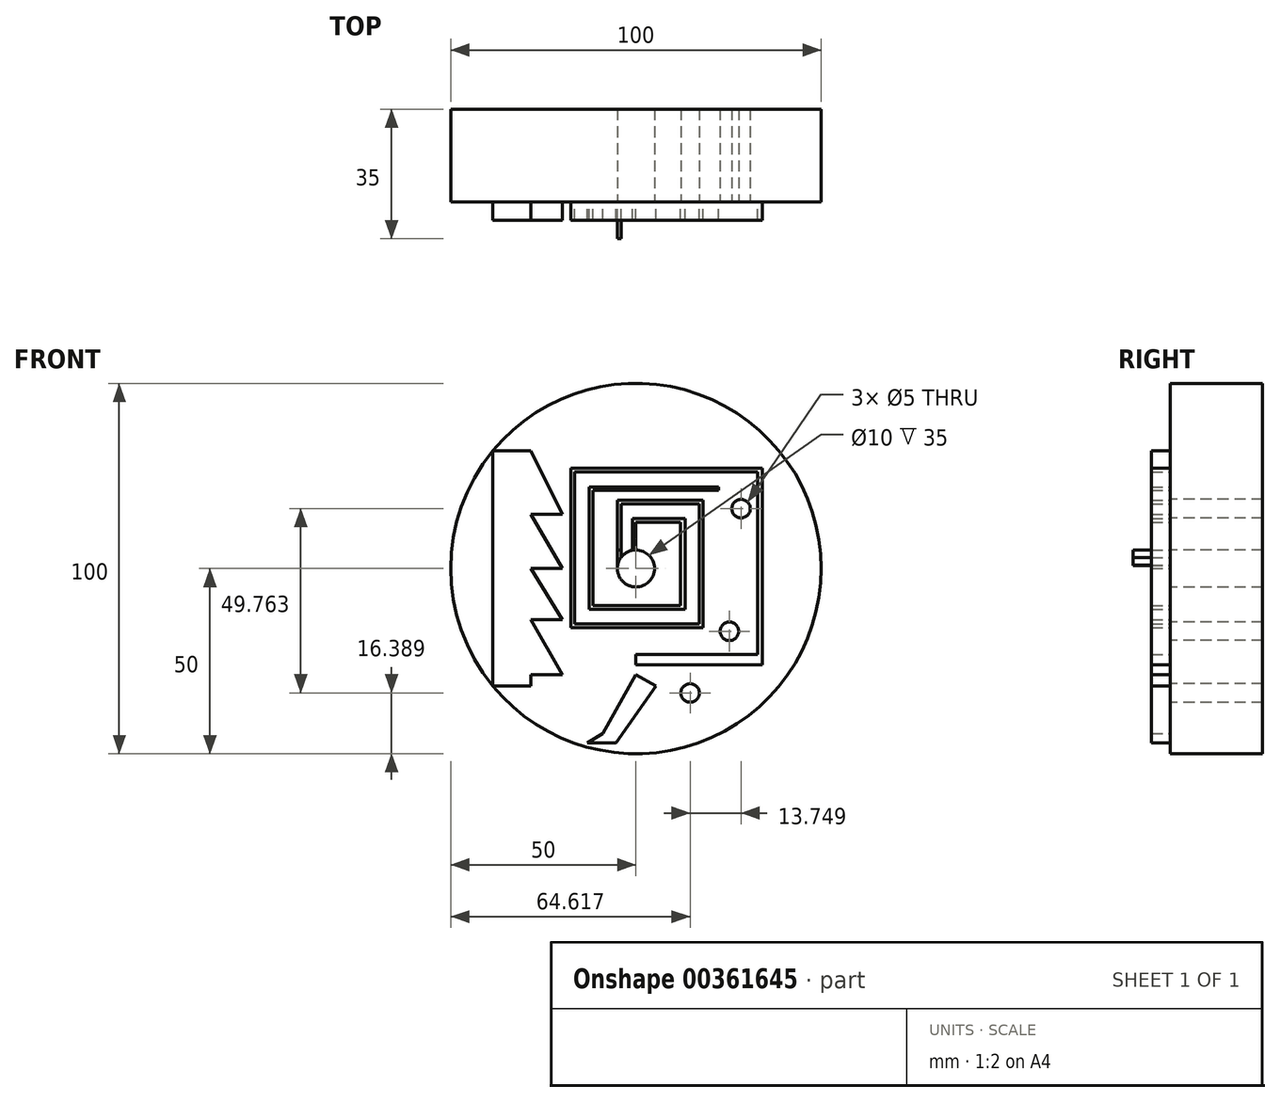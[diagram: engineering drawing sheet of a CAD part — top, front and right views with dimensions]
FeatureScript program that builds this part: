
annotation { "Feature Type Name" : "Feature", "Feature Type Description" : "" }
export const myFeature = defineFeature(function(context is Context, id is Id, definition is map)
    precondition{}
    {
        {
            var Q0;
            Q0=qCreatedBy(makeId("Front.planeOp"),FACE);
            var sketch = newSketch(context, id + "F0", { "sketchPlane" : qUnion([Q0])});
            skCircle(sketch, "E0", {"center": v(0, 0) * mm, "radius": 50 * mm});
            skSolve(sketch);
        }
        {
            var Q0;
            Q0=makeQuery(id+"F0.imprint","IMPRINT",FACE,{"disambiguationData":[TD([[makeQuery(id+"F0.imprint","IMPRINT",EDGE,{"derivedFrom":sQuery(id+"F0.wireOp",EDGE,"E0")}),1.0]])]});
            extrude(context, id + "F1", {"entities" : qUnion([Q0]), "depth" : 25 * mm});
        }
        {
            var Q0;
            Q0=makeQuery(id+"F1.opExtrude","CAP_FACE",FACE,{"disambiguationData":[OSD([sQuery(id+"F0.wireOp",EDGE,"E0")])],"isStart":false});
            var sketch = newSketch(context, id + "F2", { "sketchPlane" : qUnion([Q0])});
            skCircle(sketch, "E1", {"center": v(0, 0) * mm, "radius": 8.25 * mm});
            skSolve(sketch);
        }
        {
            var Q0;
            Q0=sQuery(id+"F2.wireOp",VERTEX,"E1.center");
            var Q1;
            Q1=makeQuery(id+"F1.opExtrude","SWEPT_BODY",BODY,{"disambiguationData":[OSD([sQuery(id+"F0.wireOp",EDGE,"E0")])]});
            hole(context, id + "F3", {"style" : HoleStyle.SIMPLE, "endStyle" : HoleEndStyle.THROUGH, "holeDiameter" : 10 * mm, "isTappedThrough" : true, "tappedDepth" : 12 * mm, "tapClearance" : 3, "locations" : qUnion([Q0]), "scope" : qUnion([Q1])});
        }
        {
            var Q0;
            Q0=makeQuery(id+"F1.opExtrude","CAP_FACE",FACE,{"disambiguationData":[OSD([sQuery(id+"F0.wireOp",EDGE,"E0")])],"isStart":false});
            var sketch = newSketch(context, id + "F4", { "sketchPlane" : qUnion([Q0])});
            skLineSegment(sketch, "E2", {"start": v(0, 5) * mm, "end": v(0, 12.48) * mm});
            skLineSegment(sketch, "E3", {"start": v(0, 12.48) * mm, "end": v(12.05, 12.48) * mm});
            skLineSegment(sketch, "E4", {"start": v(12.05, 12.48) * mm, "end": v(12.05, 0) * mm});
            skLineSegment(sketch, "E5", {"start": v(12.05, 0) * mm, "end": v(12.05, -10) * mm});
            skLineSegment(sketch, "E6", {"start": v(12.05, -10) * mm, "end": v(0, -10) * mm});
            skLineSegment(sketch, "E7", {"start": v(0, -10) * mm, "end": v(-11.6, -10) * mm});
            skLineSegment(sketch, "E8", {"start": v(-11.6, -10) * mm, "end": v(-11.6, 0) * mm});
            skLineSegment(sketch, "E9", {"start": v(-11.6, 0) * mm, "end": v(-11.6, 12.48) * mm});
            skLineSegment(sketch, "E10", {"start": v(-11.6, 12.48) * mm, "end": v(-11.6, 21.05) * mm});
            skLineSegment(sketch, "E11", {"start": v(-11.6, 21.05) * mm, "end": v(22.32, 21.05) * mm});
            skLineSegment(sketch, "E12.0", {"start": v(-16.6, 26.05) * mm, "end": v(22.32, 26.05) * mm});
            skLineSegment(sketch, "E12.1", {"start": v(-16.6, 12.48) * mm, "end": v(-16.6, 26.05) * mm});
            skLineSegment(sketch, "E12.2", {"start": v(-16.6, 0) * mm, "end": v(-16.6, 12.48) * mm});
            skLineSegment(sketch, "E12.3", {"start": v(-16.6, -15) * mm, "end": v(-16.6, 0) * mm});
            skLineSegment(sketch, "E12.4", {"start": v(0, -15) * mm, "end": v(-16.6, -15) * mm});
            skLineSegment(sketch, "E12.5", {"start": v(17.05, -15) * mm, "end": v(0, -15) * mm});
            skLineSegment(sketch, "E12.6", {"start": v(-5, 5) * mm, "end": v(-5, 17.48) * mm});
            skLineSegment(sketch, "E12.8", {"start": v(17.05, 17.48) * mm, "end": v(17.05, 0) * mm});
            skLineSegment(sketch, "E12.9", {"start": v(17.05, 0) * mm, "end": v(17.05, -15) * mm});
            skLineSegment(sketch, "E13.0", {"start": v(-16.6, 27.05) * mm, "end": v(22.32, 27.05) * mm});
            skLineSegment(sketch, "E14", {"start": v(-17.6, 26.16) * mm, "end": v(-17.6, -14.9) * mm});
            skLineSegment(sketch, "E15", {"start": v(-16.6, 27.05) * mm, "end": v(-17.6, 27.05) * mm});
            skLineSegment(sketch, "E16", {"start": v(-17.6, 27.05) * mm, "end": v(-17.6, 26.16) * mm});
            skLineSegment(sketch, "E17", {"start": v(22.32, 26.05) * mm, "end": v(22.32, 27.05) * mm});
            skLineSegment(sketch, "E18", {"start": v(-17.6, -15) * mm, "end": v(-17.6, -14.9) * mm});
            skLineSegment(sketch, "E19", {"start": v(22.32, 21.05) * mm, "end": v(22.32, 22.05) * mm});
            skLineSegment(sketch, "E20", {"start": v(22.32, 22.05) * mm, "end": v(-11.6, 22.05) * mm});
            skLineSegment(sketch, "E21", {"start": v(-11.6, 22.05) * mm, "end": v(-12.6, 22.05) * mm});
            skLineSegment(sketch, "E22", {"start": v(-12.6, 22.05) * mm, "end": v(-12.6, 5.56) * mm});
            skLineSegment(sketch, "E23", {"start": v(-12.6, 5.56) * mm, "end": v(-12.6, -11.01) * mm});
            skLineSegment(sketch, "E24", {"start": v(13.27, 12.48) * mm, "end": v(13.27, 13.48) * mm});
            skLineSegment(sketch, "E25", {"start": v(13.27, 13.48) * mm, "end": v(0, 13.48) * mm});
            skLineSegment(sketch, "E26", {"start": v(0, 13.48) * mm, "end": v(-1, 13.48) * mm});
            skLineSegment(sketch, "E27", {"start": v(-1, 13.48) * mm, "end": v(-1, 5) * mm});
            skLineSegment(sketch, "E28", {"start": v(-1, 13.48) * mm, "end": v(-1, 12.48) * mm});
            skLineSegment(sketch, "E29", {"start": v(-5, 17.48) * mm, "end": v(-5, 18.48) * mm});
            skLineSegment(sketch, "E30", {"start": v(-5, 18.48) * mm, "end": v(17.05, 18.48) * mm});
            skLineSegment(sketch, "E31", {"start": v(17.05, 18.48) * mm, "end": v(18.05, 18.48) * mm});
            skLineSegment(sketch, "E32", {"start": v(18.05, 18.48) * mm, "end": v(18.05, -15) * mm});
            skLineSegment(sketch, "E33", {"start": v(18.05, -15) * mm, "end": v(18.05, -16) * mm});
            skLineSegment(sketch, "E34", {"start": v(18.05, -16) * mm, "end": v(-17.6, -16) * mm});
            skLineSegment(sketch, "E35", {"start": v(-17.6, -16) * mm, "end": v(-17.6, -14.9) * mm});
            skLineSegment(sketch, "E36", {"start": v(13.27, 12.48) * mm, "end": v(13.27, -10) * mm});
            skLineSegment(sketch, "E37", {"start": v(13.27, -10) * mm, "end": v(13.27, -11) * mm});
            skLineSegment(sketch, "E38", {"start": v(13.27, -11) * mm, "end": v(-12.6, -11.01) * mm});
            skLineSegment(sketch, "E39", {"start": v(17.05, 17.48) * mm, "end": v(-4, 17.48) * mm});
            skLineSegment(sketch, "E40", {"start": v(-4, 17.48) * mm, "end": v(-4, 5) * mm});
            skLineSegment(sketch, "E41", {"start": v(-5, 5) * mm, "end": v(-4, 5) * mm});
            skLineSegment(sketch, "E42", {"start": v(-1, 5) * mm, "end": v(0, 5) * mm});
            skSolve(sketch);
        }
        {
            var Q0;
            Q0 = qSketchRegion(id + "F4", true);
            extrude(context, id + "F5", {"entities" : qUnion([Q0]), "operationType" : NewBodyOperationType.ADD, "depth" : 5 * mm});
        }
        {
            var Q0;
            Q0=makeQuery(id+"F1.opExtrude","CAP_FACE",FACE,{"disambiguationData":[OSD([sQuery(id+"F0.wireOp",EDGE,"E0")])],"isStart":false});
            var sketch = newSketch(context, id + "F6", { "sketchPlane" : qUnion([Q0])});
            skLineSegment(sketch, "E43", {"start": v(-5, 5) * mm, "end": v(-5, 0.76) * mm});
            skLineSegment(sketch, "E44", {"start": v(-4, 5) * mm, "end": v(-4, 3) * mm});
            skLineSegment(sketch, "E45", {"start": v(-4, 3) * mm, "end": v(-5, 0.76) * mm});
            skSolve(sketch);
        }
        {
            var Q0;
            {var subQ1=sQuery(id+"F6.wireOp",EDGE,"E43");Q0=makeQuery(id+"F6.imprint","IMPRINT",FACE,{"disambiguationData":[TD([[makeQuery(id+"F6.imprint","IMPRINT",EDGE,{"derivedFrom":subQ1}),1.0]])]});}
            extrude(context, id + "F7", {"entities" : qUnion([Q0]), "operationType" : NewBodyOperationType.ADD, "depth" : 10 * mm});
        }
        {
            var Q0;
            Q0=makeQuery(id+"F1.opExtrude","CAP_FACE",FACE,{"disambiguationData":[OSD([sQuery(id+"F0.wireOp",EDGE,"E0")])],"isStart":false});
            var sketch = newSketch(context, id + "F8", { "sketchPlane" : qUnion([Q0])});
            skLineSegment(sketch, "E46", {"start": v(22.32, 27.05) * mm, "end": v(25.6, 27.05) * mm});
            skLineSegment(sketch, "E47", {"start": v(22.32, 26.05) * mm, "end": v(25.6, 26.05) * mm});
            skLineSegment(sketch, "E48", {"start": v(22.32, 27.05) * mm, "end": v(22.32, 26.05) * mm});
            skLineSegment(sketch, "E49", {"start": v(27.15, 26.05) * mm, "end": v(25.6, 26.05) * mm});
            skLineSegment(sketch, "E50", {"start": v(25.6, 27.05) * mm, "end": v(28.47, 27.05) * mm});
            skLineSegment(sketch, "E51", {"start": v(27.15, 26.05) * mm, "end": v(28.9, 26.05) * mm});
            skLineSegment(sketch, "E52", {"start": v(28.9, 26.05) * mm, "end": v(32.89, 26.05) * mm});
            skLineSegment(sketch, "E53", {"start": v(28.47, 27.05) * mm, "end": v(32.89, 27.05) * mm});
            skLineSegment(sketch, "E54", {"start": v(32.89, 26.05) * mm, "end": v(32.89, 18.48) * mm});
            skLineSegment(sketch, "E55", {"start": v(32.89, 27.05) * mm, "end": v(34.1, 27.05) * mm});
            skLineSegment(sketch, "E56", {"start": v(34.1, 27.05) * mm, "end": v(34.1, 18.48) * mm});
            skLineSegment(sketch, "E57", {"start": v(34.1, 18.48) * mm, "end": v(34.1, 11.97) * mm});
            skLineSegment(sketch, "E58", {"start": v(32.89, 18.48) * mm, "end": v(32.89, 9.35) * mm});
            skLineSegment(sketch, "E59", {"start": v(34.1, 11.97) * mm, "end": v(34.1, 6.97) * mm});
            skLineSegment(sketch, "E60", {"start": v(32.89, 9.35) * mm, "end": v(32.89, 5.56) * mm});
            skLineSegment(sketch, "E61", {"start": v(34.1, 6.97) * mm, "end": v(34.1, 0) * mm});
            skLineSegment(sketch, "E62", {"start": v(32.89, 5.56) * mm, "end": v(32.89, 0) * mm});
            skLineSegment(sketch, "E63", {"start": v(32.89, 0) * mm, "end": v(32.89, -5.78) * mm});
            skLineSegment(sketch, "E64", {"start": v(34.1, 0) * mm, "end": v(34.1, -16) * mm});
            skLineSegment(sketch, "E65", {"start": v(32.89, -5.78) * mm, "end": v(32.89, -17.55) * mm});
            skLineSegment(sketch, "E66", {"start": v(32.89, -17.55) * mm, "end": v(32.89, -21.47) * mm});
            skLineSegment(sketch, "E67", {"start": v(34.1, -16) * mm, "end": v(34.1, -23.27) * mm});
            skLineSegment(sketch, "E68", {"start": v(32.89, -21.47) * mm, "end": v(32.89, -23.27) * mm});
            skLineSegment(sketch, "E69", {"start": v(32.89, -23.27) * mm, "end": v(34.1, -23.27) * mm});
            skSolve(sketch);
        }
        {
            var Q0;
            Q0 = qSketchRegion(id + "F8", true);
            extrude(context, id + "F9", {"entities" : qUnion([Q0]), "operationType" : NewBodyOperationType.ADD, "depth" : 5 * mm});
        }
        {
            var Q0;
            Q0=makeQuery(id+"F1.opExtrude","CAP_FACE",FACE,{"disambiguationData":[OSD([sQuery(id+"F0.wireOp",EDGE,"E0")])],"isStart":false});
            var sketch = newSketch(context, id + "F10", { "sketchPlane" : qUnion([Q0])});
            skLineSegment(sketch, "E70", {"start": v(32.89, -23.27) * mm, "end": v(0, -23.27) * mm});
            skLineSegment(sketch, "E71", {"start": v(34.1, -23.27) * mm, "end": v(34.1, -26.04) * mm});
            skLineSegment(sketch, "E72", {"start": v(34.1, -26.04) * mm, "end": v(0, -26.04) * mm});
            skLineSegment(sketch, "E73", {"start": v(0, -26.04) * mm, "end": v(0, -23.27) * mm});
            skLineSegment(sketch, "E74", {"start": v(32.89, -23.27) * mm, "end": v(34.1, -23.27) * mm});
            skSolve(sketch);
        }
        {
            var Q0;
            Q0=makeQuery(id+"F10.imprint","IMPRINT",FACE,{"disambiguationData":[TD([[makeQuery(id+"F10.imprint","IMPRINT",EDGE,{"derivedFrom":sQuery(id+"F10.wireOp",EDGE,"E70")}),1.0]])]});
            extrude(context, id + "F11", {"entities" : qUnion([Q0]), "operationType" : NewBodyOperationType.ADD, "depth" : 5 * mm});
        }
        {
            var Q0;
            Q0=makeQuery(id+"F1.opExtrude","CAP_FACE",FACE,{"disambiguationData":[OSD([sQuery(id+"F0.wireOp",EDGE,"E0")])],"isStart":false});
            var sketch = newSketch(context, id + "F12", { "sketchPlane" : qUnion([Q0])});
            skCircle(sketch, "E75", {"center": v(25.22, -16.96) * mm, "radius": 3.33 * mm});
            skCircle(sketch, "E76", {"center": v(28.37, 16.15) * mm, "radius": 2.9 * mm});
            skSolve(sketch);
        }
        {
            var Q0;
            Q0=sQuery(id+"F12.wireOp",VERTEX,"E75.center");
            var Q1;
            Q1=sQuery(id+"F12.wireOp",VERTEX,"E76.center");
            var Q2;
            Q2=makeQuery(id+"F1.opExtrude","SWEPT_BODY",BODY,{"disambiguationData":[OSD([sQuery(id+"F0.wireOp",EDGE,"E0")])]});
            hole(context, id + "F13", {"style" : HoleStyle.SIMPLE, "endStyle" : HoleEndStyle.THROUGH, "holeDiameter" : 5 * mm, "isTappedThrough" : true, "tappedDepth" : 12 * mm, "tapClearance" : 3, "locations" : qUnion([Q0, Q1]), "scope" : qUnion([Q2])});
        }
        {
            var Q0;
            Q0=makeQuery(id+"F1.opExtrude","CAP_FACE",FACE,{"disambiguationData":[OSD([sQuery(id+"F0.wireOp",EDGE,"E0")])],"isStart":false});
            var sketch = newSketch(context, id + "F14", { "sketchPlane" : qUnion([Q0])});
            skLineSegment(sketch, "E77", {"start": v(-38.64, 31.73) * mm, "end": v(-38.64, -31.73) * mm});
            skLineSegment(sketch, "E78", {"start": v(-38.64, 31.73) * mm, "end": v(-28.42, 31.73) * mm});
            skLineSegment(sketch, "E79", {"start": v(-28.42, 31.73) * mm, "end": v(-28.42, -31.03) * mm});
            skLineSegment(sketch, "E80", {"start": v(-38.64, -31.73) * mm, "end": v(-28.42, -31.73) * mm});
            skLineSegment(sketch, "E81", {"start": v(-28.42, -31.03) * mm, "end": v(-28.42, -31.73) * mm});
            skSolve(sketch);
        }
        {
            var Q0;
            Q0 = qSketchRegion(id + "F14", true);
            extrude(context, id + "F15", {"entities" : qUnion([Q0]), "operationType" : NewBodyOperationType.ADD, "depth" : 5 * mm});
        }
        {
            var Q0;
            {var subQ0=sQuery(id+"F0.wireOp",EDGE,"E0");var subQ1=makeQuery(id+"F1.opExtrude","CAP_FACE",FACE,{"disambiguationData":[OSD([subQ0])],"isStart":false});var subQ2=sQuery(id+"F3.hole-0.sketch.wireOp",EDGE,"core_line_2");Q0=makeQuery(id+"F15.boolean.opBoolean","SPLIT",FACE,{"disambiguationData":[TD([makeQuery(id+"F1.opExtrude","SWEPT_FACE",FACE,{"disambiguationData":[OSD([subQ0])]}),subQ1,makeQuery(id+"F3.hole-0.boolean.opBoolean","COPY",FACE,{"derivedFrom":makeQuery(id+"F3.hole-0.opRevolve","SWEPT_FACE",FACE,{"disambiguationData":[OSD([subQ2])]})}),makeQuery(id+"F5.opExtrude","SWEPT_FACE",FACE,{"disambiguationData":[OSD([sQuery(id+"F4.wireOp",EDGE,"E2")])]}),makeQuery(id+"F5.opExtrude","SWEPT_FACE",FACE,{"disambiguationData":[OSD([sQuery(id+"F4.wireOp",EDGE,"E3")])]}),makeQuery(id+"F5.opExtrude","SWEPT_FACE",FACE,{"disambiguationData":[OSD([sQuery(id+"F4.wireOp",EDGE,"E4"),sQuery(id+"F4.wireOp",EDGE,"E5")])]}),makeQuery(id+"F5.opExtrude","SWEPT_FACE",FACE,{"disambiguationData":[OSD([sQuery(id+"F4.wireOp",EDGE,"E6"),sQuery(id+"F4.wireOp",EDGE,"E7")])]}),makeQuery(id+"F5.opExtrude","SWEPT_FACE",FACE,{"disambiguationData":[OSD([sQuery(id+"F4.wireOp",EDGE,"E8"),sQuery(id+"F4.wireOp",EDGE,"E9"),sQuery(id+"F4.wireOp",EDGE,"E10")])]}),makeQuery(id+"F5.opExtrude","SWEPT_FACE",FACE,{"disambiguationData":[OSD([sQuery(id+"F4.wireOp",EDGE,"E11")])]}),makeQuery(id+"F5.opExtrude","SWEPT_FACE",FACE,{"disambiguationData":[OSD([sQuery(id+"F4.wireOp",EDGE,"E12.0")])]}),makeQuery(id+"F5.opExtrude","SWEPT_FACE",FACE,{"disambiguationData":[OSD([sQuery(id+"F4.wireOp",EDGE,"E12.1"),sQuery(id+"F4.wireOp",EDGE,"E12.2"),sQuery(id+"F4.wireOp",EDGE,"E12.3")])]}),makeQuery(id+"F5.opExtrude","SWEPT_FACE",FACE,{"disambiguationData":[OSD([sQuery(id+"F4.wireOp",EDGE,"E12.4"),sQuery(id+"F4.wireOp",EDGE,"E12.5")])]}),makeQuery(id+"F5.opExtrude","SWEPT_FACE",FACE,{"disambiguationData":[OSD([sQuery(id+"F4.wireOp",EDGE,"E12.6"),sQuery(id+"F4.wireOp",EDGE,"E29")])]}),makeQuery(id+"F5.opExtrude","SWEPT_FACE",FACE,{"disambiguationData":[OSD([sQuery(id+"F4.wireOp",EDGE,"E12.8"),sQuery(id+"F4.wireOp",EDGE,"E12.9")])]}),makeQuery(id+"F5.opExtrude","SWEPT_FACE",FACE,{"disambiguationData":[OSD([sQuery(id+"F4.wireOp",EDGE,"E13.0"),sQuery(id+"F4.wireOp",EDGE,"E15")])]}),makeQuery(id+"F5.opExtrude","SWEPT_FACE",FACE,{"disambiguationData":[OSD([sQuery(id+"F4.wireOp",EDGE,"E14"),sQuery(id+"F4.wireOp",EDGE,"E16"),sQuery(id+"F4.wireOp",EDGE,"E35")])]}),makeQuery(id+"F5.opExtrude","SWEPT_FACE",FACE,{"disambiguationData":[OSD([sQuery(id+"F4.wireOp",EDGE,"E19")])]}),makeQuery(id+"F5.opExtrude","SWEPT_FACE",FACE,{"disambiguationData":[OSD([sQuery(id+"F4.wireOp",EDGE,"E20"),sQuery(id+"F4.wireOp",EDGE,"E21")])]}),makeQuery(id+"F5.opExtrude","SWEPT_FACE",FACE,{"disambiguationData":[OSD([sQuery(id+"F4.wireOp",EDGE,"E22"),sQuery(id+"F4.wireOp",EDGE,"E23")])]}),makeQuery(id+"F5.opExtrude","SWEPT_FACE",FACE,{"disambiguationData":[OSD([sQuery(id+"F4.wireOp",EDGE,"E24"),sQuery(id+"F4.wireOp",EDGE,"E36"),sQuery(id+"F4.wireOp",EDGE,"E37")])]}),makeQuery(id+"F5.opExtrude","SWEPT_FACE",FACE,{"disambiguationData":[OSD([sQuery(id+"F4.wireOp",EDGE,"E25"),sQuery(id+"F4.wireOp",EDGE,"E26")])]}),makeQuery(id+"F5.opExtrude","SWEPT_FACE",FACE,{"disambiguationData":[OSD([sQuery(id+"F4.wireOp",EDGE,"E27"),sQuery(id+"F4.wireOp",EDGE,"E28")])]}),makeQuery(id+"F5.opExtrude","SWEPT_FACE",FACE,{"disambiguationData":[OSD([sQuery(id+"F4.wireOp",EDGE,"E30"),sQuery(id+"F4.wireOp",EDGE,"E31")])]}),makeQuery(id+"F5.opExtrude","SWEPT_FACE",FACE,{"disambiguationData":[OSD([sQuery(id+"F4.wireOp",EDGE,"E32"),sQuery(id+"F4.wireOp",EDGE,"E33")])]}),makeQuery(id+"F5.opExtrude","SWEPT_FACE",FACE,{"disambiguationData":[OSD([sQuery(id+"F4.wireOp",EDGE,"E34")])]}),makeQuery(id+"F5.opExtrude","SWEPT_FACE",FACE,{"disambiguationData":[OSD([sQuery(id+"F4.wireOp",EDGE,"E38")])]}),makeQuery(id+"F5.opExtrude","SWEPT_FACE",FACE,{"disambiguationData":[OSD([sQuery(id+"F4.wireOp",EDGE,"E39")])]}),makeQuery(id+"F5.opExtrude","SWEPT_FACE",FACE,{"disambiguationData":[OSD([sQuery(id+"F4.wireOp",EDGE,"E40")])]}),makeQuery(id+"F5.opExtrude","SWEPT_FACE",FACE,{"disambiguationData":[OSD([sQuery(id+"F4.wireOp",EDGE,"E42")])]}),makeQuery(id+"F7.opExtrude","SWEPT_FACE",FACE,{"disambiguationData":[OSD([sQuery(id+"F6.wireOp",EDGE,"E43")])]}),makeQuery(id+"F7.opExtrude","SWEPT_FACE",FACE,{"disambiguationData":[OSD([sQuery(id+"F6.wireOp",EDGE,"E44")])]}),makeQuery(id+"F7.opExtrude","SWEPT_FACE",FACE,{"disambiguationData":[OSD([sQuery(id+"F6.wireOp",EDGE,"E45")])]}),makeQuery(id+"F7.opExtrude","SWEPT_FACE",FACE,{"disambiguationData":[OSD([subQ2,sQuery(id+"F3.hole-0.sketch.wireOp",EDGE,"core_line_3")])]}),makeQuery(id+"F9.opExtrude","SWEPT_FACE",FACE,{"disambiguationData":[OSD([sQuery(id+"F8.wireOp",EDGE,"E46"),sQuery(id+"F8.wireOp",EDGE,"E50"),sQuery(id+"F8.wireOp",EDGE,"E53"),sQuery(id+"F8.wireOp",EDGE,"E55")])]}),makeQuery(id+"F9.opExtrude","SWEPT_FACE",FACE,{"disambiguationData":[OSD([sQuery(id+"F8.wireOp",EDGE,"E47"),sQuery(id+"F8.wireOp",EDGE,"E49"),sQuery(id+"F8.wireOp",EDGE,"E51"),sQuery(id+"F8.wireOp",EDGE,"E52")])]}),makeQuery(id+"F9.opExtrude","SWEPT_FACE",FACE,{"disambiguationData":[OSD([sQuery(id+"F8.wireOp",EDGE,"E54"),sQuery(id+"F8.wireOp",EDGE,"E58"),sQuery(id+"F8.wireOp",EDGE,"E60"),sQuery(id+"F8.wireOp",EDGE,"E62"),sQuery(id+"F8.wireOp",EDGE,"E63"),sQuery(id+"F8.wireOp",EDGE,"E65"),sQuery(id+"F8.wireOp",EDGE,"E66"),sQuery(id+"F8.wireOp",EDGE,"E68")])]}),makeQuery(id+"F9.opExtrude","SWEPT_FACE",FACE,{"disambiguationData":[OSD([sQuery(id+"F8.wireOp",EDGE,"E56"),sQuery(id+"F8.wireOp",EDGE,"E57"),sQuery(id+"F8.wireOp",EDGE,"E59"),sQuery(id+"F8.wireOp",EDGE,"E61"),sQuery(id+"F8.wireOp",EDGE,"E64"),sQuery(id+"F8.wireOp",EDGE,"E67")])]}),makeQuery(id+"F11.opExtrude","SWEPT_FACE",FACE,{"disambiguationData":[OSD([sQuery(id+"F10.wireOp",EDGE,"E70"),sQuery(id+"F10.wireOp",EDGE,"E74")])]}),makeQuery(id+"F11.opExtrude","SWEPT_FACE",FACE,{"disambiguationData":[OSD([sQuery(id+"F10.wireOp",EDGE,"E71")])]}),makeQuery(id+"F11.opExtrude","SWEPT_FACE",FACE,{"disambiguationData":[OSD([sQuery(id+"F10.wireOp",EDGE,"E72")])]}),makeQuery(id+"F11.opExtrude","SWEPT_FACE",FACE,{"disambiguationData":[OSD([sQuery(id+"F10.wireOp",EDGE,"E73")])]}),makeQuery(id+"F13.hole-0.boolean.opBoolean","COPY",FACE,{"derivedFrom":makeQuery(id+"F13.hole-0.opRevolve","SWEPT_FACE",FACE,{"disambiguationData":[OSD([sQuery(id+"F13.hole-0.sketch.wireOp",EDGE,"core_line_2")])]})}),makeQuery(id+"F13.hole-1.boolean.opBoolean","COPY",FACE,{"derivedFrom":makeQuery(id+"F13.hole-1.opRevolve","SWEPT_FACE",FACE,{"disambiguationData":[OSD([sQuery(id+"F13.hole-1.sketch.wireOp",EDGE,"core_line_2")])]})}),makeQuery(id+"F15.opExtrude","SWEPT_FACE",FACE,{"disambiguationData":[OSD([sQuery(id+"F14.wireOp",EDGE,"E77")])]}),makeQuery(id+"F15.opExtrude","SWEPT_FACE",FACE,{"disambiguationData":[OSD([sQuery(id+"F14.wireOp",EDGE,"E78")])]}),makeQuery(id+"F15.opExtrude","SWEPT_FACE",FACE,{"disambiguationData":[OSD([sQuery(id+"F14.wireOp",EDGE,"E79"),sQuery(id+"F14.wireOp",EDGE,"E81")])]}),makeQuery(id+"F15.opExtrude","SWEPT_FACE",FACE,{"disambiguationData":[OSD([sQuery(id+"F14.wireOp",EDGE,"E80")])]})])],"derivedFrom":subQ1});}
            var sketch = newSketch(context, id + "F16", { "sketchPlane" : qUnion([Q0])});
            skLineSegment(sketch, "E82", {"start": v(-28.42, 31.73) * mm, "end": v(-19.87, 14.57) * mm});
            skLineSegment(sketch, "E83", {"start": v(-28.42, 31.73) * mm, "end": v(-28.42, 14.57) * mm});
            skLineSegment(sketch, "E84", {"start": v(-28.42, 14.57) * mm, "end": v(-19.87, 14.57) * mm});
            skLineSegment(sketch, "E85", {"start": v(-28.42, 14.57) * mm, "end": v(-28.42, 0) * mm});
            skLineSegment(sketch, "E86", {"start": v(-28.42, 0) * mm, "end": v(-19.87, 0) * mm});
            skLineSegment(sketch, "E87", {"start": v(-19.87, 0) * mm, "end": v(-28.42, 14.57) * mm});
            skLineSegment(sketch, "E88", {"start": v(-28.42, 0) * mm, "end": v(-28.42, -13.84) * mm});
            skLineSegment(sketch, "E89", {"start": v(-28.42, -13.84) * mm, "end": v(-19.87, -13.84) * mm});
            skLineSegment(sketch, "E90", {"start": v(-19.87, -13.84) * mm, "end": v(-28.42, 0) * mm});
            skLineSegment(sketch, "E91", {"start": v(-28.42, -13.84) * mm, "end": v(-28.42, -28.66) * mm});
            skLineSegment(sketch, "E92", {"start": v(-28.42, -28.66) * mm, "end": v(-19.87, -28.66) * mm});
            skLineSegment(sketch, "E93", {"start": v(-19.87, -28.66) * mm, "end": v(-28.42, -13.84) * mm});
            skSolve(sketch);
        }
        {
            var Q0;
            Q0 = qSketchRegion(id + "F16", true);
            extrude(context, id + "F17", {"entities" : qUnion([Q0]), "operationType" : NewBodyOperationType.ADD, "depth" : 5 * mm});
        }
        {
            var Q0;
            {var subQ0=sQuery(id+"F0.wireOp",EDGE,"E0");var subQ1=makeQuery(id+"F1.opExtrude","CAP_FACE",FACE,{"disambiguationData":[OSD([subQ0])],"isStart":false});var subQ2=sQuery(id+"F3.hole-0.sketch.wireOp",EDGE,"core_line_2");Q0=makeQuery(id+"F15.boolean.opBoolean","SPLIT",FACE,{"disambiguationData":[TD([makeQuery(id+"F1.opExtrude","SWEPT_FACE",FACE,{"disambiguationData":[OSD([subQ0])]}),subQ1,makeQuery(id+"F3.hole-0.boolean.opBoolean","COPY",FACE,{"derivedFrom":makeQuery(id+"F3.hole-0.opRevolve","SWEPT_FACE",FACE,{"disambiguationData":[OSD([subQ2])]})}),makeQuery(id+"F5.opExtrude","SWEPT_FACE",FACE,{"disambiguationData":[OSD([sQuery(id+"F4.wireOp",EDGE,"E2")])]}),makeQuery(id+"F5.opExtrude","SWEPT_FACE",FACE,{"disambiguationData":[OSD([sQuery(id+"F4.wireOp",EDGE,"E3")])]}),makeQuery(id+"F5.opExtrude","SWEPT_FACE",FACE,{"disambiguationData":[OSD([sQuery(id+"F4.wireOp",EDGE,"E4"),sQuery(id+"F4.wireOp",EDGE,"E5")])]}),makeQuery(id+"F5.opExtrude","SWEPT_FACE",FACE,{"disambiguationData":[OSD([sQuery(id+"F4.wireOp",EDGE,"E6"),sQuery(id+"F4.wireOp",EDGE,"E7")])]}),makeQuery(id+"F5.opExtrude","SWEPT_FACE",FACE,{"disambiguationData":[OSD([sQuery(id+"F4.wireOp",EDGE,"E8"),sQuery(id+"F4.wireOp",EDGE,"E9"),sQuery(id+"F4.wireOp",EDGE,"E10")])]}),makeQuery(id+"F5.opExtrude","SWEPT_FACE",FACE,{"disambiguationData":[OSD([sQuery(id+"F4.wireOp",EDGE,"E11")])]}),makeQuery(id+"F5.opExtrude","SWEPT_FACE",FACE,{"disambiguationData":[OSD([sQuery(id+"F4.wireOp",EDGE,"E12.0")])]}),makeQuery(id+"F5.opExtrude","SWEPT_FACE",FACE,{"disambiguationData":[OSD([sQuery(id+"F4.wireOp",EDGE,"E12.1"),sQuery(id+"F4.wireOp",EDGE,"E12.2"),sQuery(id+"F4.wireOp",EDGE,"E12.3")])]}),makeQuery(id+"F5.opExtrude","SWEPT_FACE",FACE,{"disambiguationData":[OSD([sQuery(id+"F4.wireOp",EDGE,"E12.4"),sQuery(id+"F4.wireOp",EDGE,"E12.5")])]}),makeQuery(id+"F5.opExtrude","SWEPT_FACE",FACE,{"disambiguationData":[OSD([sQuery(id+"F4.wireOp",EDGE,"E12.6"),sQuery(id+"F4.wireOp",EDGE,"E29")])]}),makeQuery(id+"F5.opExtrude","SWEPT_FACE",FACE,{"disambiguationData":[OSD([sQuery(id+"F4.wireOp",EDGE,"E12.8"),sQuery(id+"F4.wireOp",EDGE,"E12.9")])]}),makeQuery(id+"F5.opExtrude","SWEPT_FACE",FACE,{"disambiguationData":[OSD([sQuery(id+"F4.wireOp",EDGE,"E13.0"),sQuery(id+"F4.wireOp",EDGE,"E15")])]}),makeQuery(id+"F5.opExtrude","SWEPT_FACE",FACE,{"disambiguationData":[OSD([sQuery(id+"F4.wireOp",EDGE,"E14"),sQuery(id+"F4.wireOp",EDGE,"E16"),sQuery(id+"F4.wireOp",EDGE,"E35")])]}),makeQuery(id+"F5.opExtrude","SWEPT_FACE",FACE,{"disambiguationData":[OSD([sQuery(id+"F4.wireOp",EDGE,"E19")])]}),makeQuery(id+"F5.opExtrude","SWEPT_FACE",FACE,{"disambiguationData":[OSD([sQuery(id+"F4.wireOp",EDGE,"E20"),sQuery(id+"F4.wireOp",EDGE,"E21")])]}),makeQuery(id+"F5.opExtrude","SWEPT_FACE",FACE,{"disambiguationData":[OSD([sQuery(id+"F4.wireOp",EDGE,"E22"),sQuery(id+"F4.wireOp",EDGE,"E23")])]}),makeQuery(id+"F5.opExtrude","SWEPT_FACE",FACE,{"disambiguationData":[OSD([sQuery(id+"F4.wireOp",EDGE,"E24"),sQuery(id+"F4.wireOp",EDGE,"E36"),sQuery(id+"F4.wireOp",EDGE,"E37")])]}),makeQuery(id+"F5.opExtrude","SWEPT_FACE",FACE,{"disambiguationData":[OSD([sQuery(id+"F4.wireOp",EDGE,"E25"),sQuery(id+"F4.wireOp",EDGE,"E26")])]}),makeQuery(id+"F5.opExtrude","SWEPT_FACE",FACE,{"disambiguationData":[OSD([sQuery(id+"F4.wireOp",EDGE,"E27"),sQuery(id+"F4.wireOp",EDGE,"E28")])]}),makeQuery(id+"F5.opExtrude","SWEPT_FACE",FACE,{"disambiguationData":[OSD([sQuery(id+"F4.wireOp",EDGE,"E30"),sQuery(id+"F4.wireOp",EDGE,"E31")])]}),makeQuery(id+"F5.opExtrude","SWEPT_FACE",FACE,{"disambiguationData":[OSD([sQuery(id+"F4.wireOp",EDGE,"E32"),sQuery(id+"F4.wireOp",EDGE,"E33")])]}),makeQuery(id+"F5.opExtrude","SWEPT_FACE",FACE,{"disambiguationData":[OSD([sQuery(id+"F4.wireOp",EDGE,"E34")])]}),makeQuery(id+"F5.opExtrude","SWEPT_FACE",FACE,{"disambiguationData":[OSD([sQuery(id+"F4.wireOp",EDGE,"E38")])]}),makeQuery(id+"F5.opExtrude","SWEPT_FACE",FACE,{"disambiguationData":[OSD([sQuery(id+"F4.wireOp",EDGE,"E39")])]}),makeQuery(id+"F5.opExtrude","SWEPT_FACE",FACE,{"disambiguationData":[OSD([sQuery(id+"F4.wireOp",EDGE,"E40")])]}),makeQuery(id+"F5.opExtrude","SWEPT_FACE",FACE,{"disambiguationData":[OSD([sQuery(id+"F4.wireOp",EDGE,"E42")])]}),makeQuery(id+"F7.opExtrude","SWEPT_FACE",FACE,{"disambiguationData":[OSD([sQuery(id+"F6.wireOp",EDGE,"E43")])]}),makeQuery(id+"F7.opExtrude","SWEPT_FACE",FACE,{"disambiguationData":[OSD([sQuery(id+"F6.wireOp",EDGE,"E44")])]}),makeQuery(id+"F7.opExtrude","SWEPT_FACE",FACE,{"disambiguationData":[OSD([sQuery(id+"F6.wireOp",EDGE,"E45")])]}),makeQuery(id+"F7.opExtrude","SWEPT_FACE",FACE,{"disambiguationData":[OSD([subQ2,sQuery(id+"F3.hole-0.sketch.wireOp",EDGE,"core_line_3")])]}),makeQuery(id+"F9.opExtrude","SWEPT_FACE",FACE,{"disambiguationData":[OSD([sQuery(id+"F8.wireOp",EDGE,"E46"),sQuery(id+"F8.wireOp",EDGE,"E50"),sQuery(id+"F8.wireOp",EDGE,"E53"),sQuery(id+"F8.wireOp",EDGE,"E55")])]}),makeQuery(id+"F9.opExtrude","SWEPT_FACE",FACE,{"disambiguationData":[OSD([sQuery(id+"F8.wireOp",EDGE,"E47"),sQuery(id+"F8.wireOp",EDGE,"E49"),sQuery(id+"F8.wireOp",EDGE,"E51"),sQuery(id+"F8.wireOp",EDGE,"E52")])]}),makeQuery(id+"F9.opExtrude","SWEPT_FACE",FACE,{"disambiguationData":[OSD([sQuery(id+"F8.wireOp",EDGE,"E54"),sQuery(id+"F8.wireOp",EDGE,"E58"),sQuery(id+"F8.wireOp",EDGE,"E60"),sQuery(id+"F8.wireOp",EDGE,"E62"),sQuery(id+"F8.wireOp",EDGE,"E63"),sQuery(id+"F8.wireOp",EDGE,"E65"),sQuery(id+"F8.wireOp",EDGE,"E66"),sQuery(id+"F8.wireOp",EDGE,"E68")])]}),makeQuery(id+"F9.opExtrude","SWEPT_FACE",FACE,{"disambiguationData":[OSD([sQuery(id+"F8.wireOp",EDGE,"E56"),sQuery(id+"F8.wireOp",EDGE,"E57"),sQuery(id+"F8.wireOp",EDGE,"E59"),sQuery(id+"F8.wireOp",EDGE,"E61"),sQuery(id+"F8.wireOp",EDGE,"E64"),sQuery(id+"F8.wireOp",EDGE,"E67")])]}),makeQuery(id+"F11.opExtrude","SWEPT_FACE",FACE,{"disambiguationData":[OSD([sQuery(id+"F10.wireOp",EDGE,"E70"),sQuery(id+"F10.wireOp",EDGE,"E74")])]}),makeQuery(id+"F11.opExtrude","SWEPT_FACE",FACE,{"disambiguationData":[OSD([sQuery(id+"F10.wireOp",EDGE,"E71")])]}),makeQuery(id+"F11.opExtrude","SWEPT_FACE",FACE,{"disambiguationData":[OSD([sQuery(id+"F10.wireOp",EDGE,"E72")])]}),makeQuery(id+"F11.opExtrude","SWEPT_FACE",FACE,{"disambiguationData":[OSD([sQuery(id+"F10.wireOp",EDGE,"E73")])]}),makeQuery(id+"F13.hole-0.boolean.opBoolean","COPY",FACE,{"derivedFrom":makeQuery(id+"F13.hole-0.opRevolve","SWEPT_FACE",FACE,{"disambiguationData":[OSD([sQuery(id+"F13.hole-0.sketch.wireOp",EDGE,"core_line_2")])]})}),makeQuery(id+"F13.hole-1.boolean.opBoolean","COPY",FACE,{"derivedFrom":makeQuery(id+"F13.hole-1.opRevolve","SWEPT_FACE",FACE,{"disambiguationData":[OSD([sQuery(id+"F13.hole-1.sketch.wireOp",EDGE,"core_line_2")])]})}),makeQuery(id+"F15.opExtrude","SWEPT_FACE",FACE,{"disambiguationData":[OSD([sQuery(id+"F14.wireOp",EDGE,"E77")])]}),makeQuery(id+"F15.opExtrude","SWEPT_FACE",FACE,{"disambiguationData":[OSD([sQuery(id+"F14.wireOp",EDGE,"E78")])]}),makeQuery(id+"F15.opExtrude","SWEPT_FACE",FACE,{"disambiguationData":[OSD([sQuery(id+"F14.wireOp",EDGE,"E79"),sQuery(id+"F14.wireOp",EDGE,"E81")])]}),makeQuery(id+"F15.opExtrude","SWEPT_FACE",FACE,{"disambiguationData":[OSD([sQuery(id+"F14.wireOp",EDGE,"E80")])]})])],"derivedFrom":subQ1});}
            var sketch = newSketch(context, id + "F18", { "sketchPlane" : qUnion([Q0])});
            skLineSegment(sketch, "E94", {"start": v(-27.22, -33.65) * mm, "end": v(-13.09, -47.13) * mm});
            skLineSegment(sketch, "E95", {"start": v(-13.09, -47.13) * mm, "end": v(-27.22, -33.65) * mm});
            skLineSegment(sketch, "E96", {"start": v(-27.22, -33.65) * mm, "end": v(-23.96, -30.23) * mm});
            skLineSegment(sketch, "E97", {"start": v(-23.96, -30.23) * mm, "end": v(-9, -44.52) * mm});
            skLineSegment(sketch, "E98", {"start": v(-9, -44.52) * mm, "end": v(-13.09, -47.13) * mm});
            skLineSegment(sketch, "E99", {"start": v(-9, -44.52) * mm, "end": v(0, -28.66) * mm});
            skLineSegment(sketch, "E100", {"start": v(0, -28.66) * mm, "end": v(5.42, -31.73) * mm});
            skLineSegment(sketch, "E101", {"start": v(5.42, -31.73) * mm, "end": v(-5.4, -47.13) * mm});
            skLineSegment(sketch, "E102", {"start": v(-5.4, -47.13) * mm, "end": v(-13.09, -47.13) * mm});
            skSolve(sketch);
        }
        {
            var Q0;
            Q0=makeQuery(id+"F18.imprint","IMPRINT",FACE,{"disambiguationData":[TD([[makeQuery(id+"F18.imprint","IMPRINT",EDGE,{"derivedFrom":sQuery(id+"F18.wireOp",EDGE,"E95")}),-1.0]])]});
            var Q1;
            Q1=makeQuery(id+"F18.imprint","IMPRINT",FACE,{"disambiguationData":[TD([[makeQuery(id+"F18.imprint","IMPRINT",EDGE,{"derivedFrom":sQuery(id+"F18.wireOp",EDGE,"E98")}),1.0]])]});
            extrude(context, id + "F19", {"entities" : qUnion([Q0, Q1]), "operationType" : NewBodyOperationType.ADD, "depth" : 5 * mm});
        }
        {
            var Q0;
            {var subQ0=sQuery(id+"F0.wireOp",EDGE,"E0");var subQ1=makeQuery(id+"F1.opExtrude","CAP_FACE",FACE,{"disambiguationData":[OSD([subQ0])],"isStart":false});var subQ2=sQuery(id+"F3.hole-0.sketch.wireOp",EDGE,"core_line_2");Q0=makeQuery(id+"F15.boolean.opBoolean","SPLIT",FACE,{"disambiguationData":[TD([makeQuery(id+"F1.opExtrude","SWEPT_FACE",FACE,{"disambiguationData":[OSD([subQ0])]}),subQ1,makeQuery(id+"F3.hole-0.boolean.opBoolean","COPY",FACE,{"derivedFrom":makeQuery(id+"F3.hole-0.opRevolve","SWEPT_FACE",FACE,{"disambiguationData":[OSD([subQ2])]})}),makeQuery(id+"F5.opExtrude","SWEPT_FACE",FACE,{"disambiguationData":[OSD([sQuery(id+"F4.wireOp",EDGE,"E2")])]}),makeQuery(id+"F5.opExtrude","SWEPT_FACE",FACE,{"disambiguationData":[OSD([sQuery(id+"F4.wireOp",EDGE,"E3")])]}),makeQuery(id+"F5.opExtrude","SWEPT_FACE",FACE,{"disambiguationData":[OSD([sQuery(id+"F4.wireOp",EDGE,"E4"),sQuery(id+"F4.wireOp",EDGE,"E5")])]}),makeQuery(id+"F5.opExtrude","SWEPT_FACE",FACE,{"disambiguationData":[OSD([sQuery(id+"F4.wireOp",EDGE,"E6"),sQuery(id+"F4.wireOp",EDGE,"E7")])]}),makeQuery(id+"F5.opExtrude","SWEPT_FACE",FACE,{"disambiguationData":[OSD([sQuery(id+"F4.wireOp",EDGE,"E8"),sQuery(id+"F4.wireOp",EDGE,"E9"),sQuery(id+"F4.wireOp",EDGE,"E10")])]}),makeQuery(id+"F5.opExtrude","SWEPT_FACE",FACE,{"disambiguationData":[OSD([sQuery(id+"F4.wireOp",EDGE,"E11")])]}),makeQuery(id+"F5.opExtrude","SWEPT_FACE",FACE,{"disambiguationData":[OSD([sQuery(id+"F4.wireOp",EDGE,"E12.0")])]}),makeQuery(id+"F5.opExtrude","SWEPT_FACE",FACE,{"disambiguationData":[OSD([sQuery(id+"F4.wireOp",EDGE,"E12.1"),sQuery(id+"F4.wireOp",EDGE,"E12.2"),sQuery(id+"F4.wireOp",EDGE,"E12.3")])]}),makeQuery(id+"F5.opExtrude","SWEPT_FACE",FACE,{"disambiguationData":[OSD([sQuery(id+"F4.wireOp",EDGE,"E12.4"),sQuery(id+"F4.wireOp",EDGE,"E12.5")])]}),makeQuery(id+"F5.opExtrude","SWEPT_FACE",FACE,{"disambiguationData":[OSD([sQuery(id+"F4.wireOp",EDGE,"E12.6"),sQuery(id+"F4.wireOp",EDGE,"E29")])]}),makeQuery(id+"F5.opExtrude","SWEPT_FACE",FACE,{"disambiguationData":[OSD([sQuery(id+"F4.wireOp",EDGE,"E12.8"),sQuery(id+"F4.wireOp",EDGE,"E12.9")])]}),makeQuery(id+"F5.opExtrude","SWEPT_FACE",FACE,{"disambiguationData":[OSD([sQuery(id+"F4.wireOp",EDGE,"E13.0"),sQuery(id+"F4.wireOp",EDGE,"E15")])]}),makeQuery(id+"F5.opExtrude","SWEPT_FACE",FACE,{"disambiguationData":[OSD([sQuery(id+"F4.wireOp",EDGE,"E14"),sQuery(id+"F4.wireOp",EDGE,"E16"),sQuery(id+"F4.wireOp",EDGE,"E35")])]}),makeQuery(id+"F5.opExtrude","SWEPT_FACE",FACE,{"disambiguationData":[OSD([sQuery(id+"F4.wireOp",EDGE,"E19")])]}),makeQuery(id+"F5.opExtrude","SWEPT_FACE",FACE,{"disambiguationData":[OSD([sQuery(id+"F4.wireOp",EDGE,"E20"),sQuery(id+"F4.wireOp",EDGE,"E21")])]}),makeQuery(id+"F5.opExtrude","SWEPT_FACE",FACE,{"disambiguationData":[OSD([sQuery(id+"F4.wireOp",EDGE,"E22"),sQuery(id+"F4.wireOp",EDGE,"E23")])]}),makeQuery(id+"F5.opExtrude","SWEPT_FACE",FACE,{"disambiguationData":[OSD([sQuery(id+"F4.wireOp",EDGE,"E24"),sQuery(id+"F4.wireOp",EDGE,"E36"),sQuery(id+"F4.wireOp",EDGE,"E37")])]}),makeQuery(id+"F5.opExtrude","SWEPT_FACE",FACE,{"disambiguationData":[OSD([sQuery(id+"F4.wireOp",EDGE,"E25"),sQuery(id+"F4.wireOp",EDGE,"E26")])]}),makeQuery(id+"F5.opExtrude","SWEPT_FACE",FACE,{"disambiguationData":[OSD([sQuery(id+"F4.wireOp",EDGE,"E27"),sQuery(id+"F4.wireOp",EDGE,"E28")])]}),makeQuery(id+"F5.opExtrude","SWEPT_FACE",FACE,{"disambiguationData":[OSD([sQuery(id+"F4.wireOp",EDGE,"E30"),sQuery(id+"F4.wireOp",EDGE,"E31")])]}),makeQuery(id+"F5.opExtrude","SWEPT_FACE",FACE,{"disambiguationData":[OSD([sQuery(id+"F4.wireOp",EDGE,"E32"),sQuery(id+"F4.wireOp",EDGE,"E33")])]}),makeQuery(id+"F5.opExtrude","SWEPT_FACE",FACE,{"disambiguationData":[OSD([sQuery(id+"F4.wireOp",EDGE,"E34")])]}),makeQuery(id+"F5.opExtrude","SWEPT_FACE",FACE,{"disambiguationData":[OSD([sQuery(id+"F4.wireOp",EDGE,"E38")])]}),makeQuery(id+"F5.opExtrude","SWEPT_FACE",FACE,{"disambiguationData":[OSD([sQuery(id+"F4.wireOp",EDGE,"E39")])]}),makeQuery(id+"F5.opExtrude","SWEPT_FACE",FACE,{"disambiguationData":[OSD([sQuery(id+"F4.wireOp",EDGE,"E40")])]}),makeQuery(id+"F5.opExtrude","SWEPT_FACE",FACE,{"disambiguationData":[OSD([sQuery(id+"F4.wireOp",EDGE,"E42")])]}),makeQuery(id+"F7.opExtrude","SWEPT_FACE",FACE,{"disambiguationData":[OSD([sQuery(id+"F6.wireOp",EDGE,"E43")])]}),makeQuery(id+"F7.opExtrude","SWEPT_FACE",FACE,{"disambiguationData":[OSD([sQuery(id+"F6.wireOp",EDGE,"E44")])]}),makeQuery(id+"F7.opExtrude","SWEPT_FACE",FACE,{"disambiguationData":[OSD([sQuery(id+"F6.wireOp",EDGE,"E45")])]}),makeQuery(id+"F7.opExtrude","SWEPT_FACE",FACE,{"disambiguationData":[OSD([subQ2,sQuery(id+"F3.hole-0.sketch.wireOp",EDGE,"core_line_3")])]}),makeQuery(id+"F9.opExtrude","SWEPT_FACE",FACE,{"disambiguationData":[OSD([sQuery(id+"F8.wireOp",EDGE,"E46"),sQuery(id+"F8.wireOp",EDGE,"E50"),sQuery(id+"F8.wireOp",EDGE,"E53"),sQuery(id+"F8.wireOp",EDGE,"E55")])]}),makeQuery(id+"F9.opExtrude","SWEPT_FACE",FACE,{"disambiguationData":[OSD([sQuery(id+"F8.wireOp",EDGE,"E47"),sQuery(id+"F8.wireOp",EDGE,"E49"),sQuery(id+"F8.wireOp",EDGE,"E51"),sQuery(id+"F8.wireOp",EDGE,"E52")])]}),makeQuery(id+"F9.opExtrude","SWEPT_FACE",FACE,{"disambiguationData":[OSD([sQuery(id+"F8.wireOp",EDGE,"E54"),sQuery(id+"F8.wireOp",EDGE,"E58"),sQuery(id+"F8.wireOp",EDGE,"E60"),sQuery(id+"F8.wireOp",EDGE,"E62"),sQuery(id+"F8.wireOp",EDGE,"E63"),sQuery(id+"F8.wireOp",EDGE,"E65"),sQuery(id+"F8.wireOp",EDGE,"E66"),sQuery(id+"F8.wireOp",EDGE,"E68")])]}),makeQuery(id+"F9.opExtrude","SWEPT_FACE",FACE,{"disambiguationData":[OSD([sQuery(id+"F8.wireOp",EDGE,"E56"),sQuery(id+"F8.wireOp",EDGE,"E57"),sQuery(id+"F8.wireOp",EDGE,"E59"),sQuery(id+"F8.wireOp",EDGE,"E61"),sQuery(id+"F8.wireOp",EDGE,"E64"),sQuery(id+"F8.wireOp",EDGE,"E67")])]}),makeQuery(id+"F11.opExtrude","SWEPT_FACE",FACE,{"disambiguationData":[OSD([sQuery(id+"F10.wireOp",EDGE,"E70"),sQuery(id+"F10.wireOp",EDGE,"E74")])]}),makeQuery(id+"F11.opExtrude","SWEPT_FACE",FACE,{"disambiguationData":[OSD([sQuery(id+"F10.wireOp",EDGE,"E71")])]}),makeQuery(id+"F11.opExtrude","SWEPT_FACE",FACE,{"disambiguationData":[OSD([sQuery(id+"F10.wireOp",EDGE,"E72")])]}),makeQuery(id+"F11.opExtrude","SWEPT_FACE",FACE,{"disambiguationData":[OSD([sQuery(id+"F10.wireOp",EDGE,"E73")])]}),makeQuery(id+"F13.hole-0.boolean.opBoolean","COPY",FACE,{"derivedFrom":makeQuery(id+"F13.hole-0.opRevolve","SWEPT_FACE",FACE,{"disambiguationData":[OSD([sQuery(id+"F13.hole-0.sketch.wireOp",EDGE,"core_line_2")])]})}),makeQuery(id+"F13.hole-1.boolean.opBoolean","COPY",FACE,{"derivedFrom":makeQuery(id+"F13.hole-1.opRevolve","SWEPT_FACE",FACE,{"disambiguationData":[OSD([sQuery(id+"F13.hole-1.sketch.wireOp",EDGE,"core_line_2")])]})}),makeQuery(id+"F15.opExtrude","SWEPT_FACE",FACE,{"disambiguationData":[OSD([sQuery(id+"F14.wireOp",EDGE,"E77")])]}),makeQuery(id+"F15.opExtrude","SWEPT_FACE",FACE,{"disambiguationData":[OSD([sQuery(id+"F14.wireOp",EDGE,"E78")])]}),makeQuery(id+"F15.opExtrude","SWEPT_FACE",FACE,{"disambiguationData":[OSD([sQuery(id+"F14.wireOp",EDGE,"E79"),sQuery(id+"F14.wireOp",EDGE,"E81")])]}),makeQuery(id+"F15.opExtrude","SWEPT_FACE",FACE,{"disambiguationData":[OSD([sQuery(id+"F14.wireOp",EDGE,"E80")])]})])],"derivedFrom":subQ1});}
            var sketch = newSketch(context, id + "F20", { "sketchPlane" : qUnion([Q0])});
            skCircle(sketch, "E103", {"center": v(14.62, -33.61) * mm, "radius": 4.88 * mm});
            skSolve(sketch);
        }
        {
            var Q0;
            Q0=sQuery(id+"F20.wireOp",VERTEX,"E103.center");
            var Q1;
            Q1=makeQuery(id+"F1.opExtrude","SWEPT_BODY",BODY,{"disambiguationData":[OSD([sQuery(id+"F0.wireOp",EDGE,"E0")])]});
            hole(context, id + "F21", {"style" : HoleStyle.SIMPLE, "endStyle" : HoleEndStyle.THROUGH, "holeDiameter" : 5 * mm, "isTappedThrough" : true, "tappedDepth" : 12 * mm, "tapClearance" : 3, "locations" : qUnion([Q0]), "scope" : qUnion([Q1])});
        }
    });
